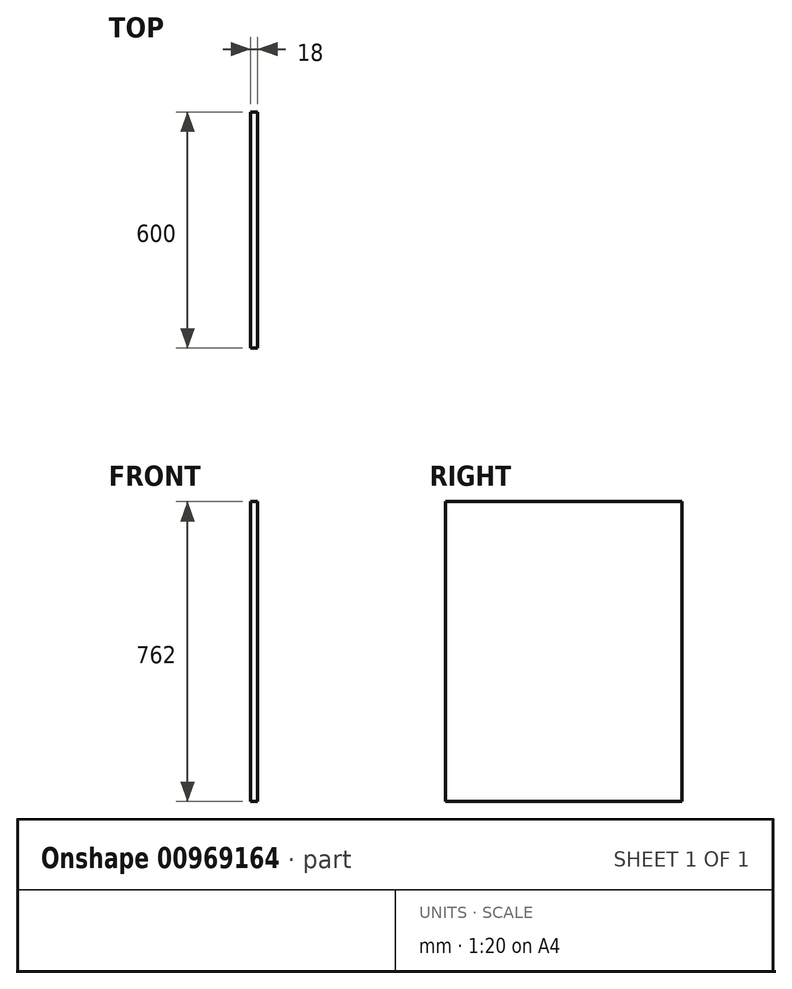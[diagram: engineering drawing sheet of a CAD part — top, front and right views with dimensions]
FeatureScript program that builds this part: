
annotation { "Feature Type Name" : "Feature", "Feature Type Description" : "" }
export const myFeature = defineFeature(function(context is Context, id is Id, definition is map)
    precondition{}
    {
        {
            var Q0;
            Q0=qCreatedBy(makeId("Right.planeOp"),FACE);
            var sketch = newSketch(context, id + "F0", { "sketchPlane" : qUnion([Q0])});
            skLineSegment(sketch, "E0.bottom", {"start": v(0, 0) * mm, "end": v(600, 0) * mm});
            skLineSegment(sketch, "E0.top", {"start": v(0, 762) * mm, "end": v(600, 762) * mm});
            skLineSegment(sketch, "E0.left", {"start": v(0, 0) * mm, "end": v(0, 762) * mm});
            skLineSegment(sketch, "E0.right", {"start": v(600, 0) * mm, "end": v(600, 762) * mm});
            skSolve(sketch);
        }
        {
            var Q0;
            Q0 = qSketchRegion(id + "F0", true);
            extrude(context, id + "F1", {"entities" : qUnion([Q0]), "depth" : 18 * mm, "offsetDistance" : 25 * mm});
        }
    });
